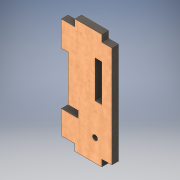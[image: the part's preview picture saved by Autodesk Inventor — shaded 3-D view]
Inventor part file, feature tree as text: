
AUTODESK INVENTOR PART (.ipt)
format: ipt  version: 2019 (Build 230136000, 136)  size: 162,816 bytes
history: native  units: mm
features: extrude x3, sketch x3, other x1
ambient origin geometry x8: Origin, YZ Plane, XZ Plane, XY Plane, X Axis, Y Axis, Z Axis, Center Point
bodies: Body1 (feature_tree)
feature tree (7):
  other  "Твердое тело1"
  extrude  "Выдавливание1"  Depth=16.0mm
  extrude  "Выдавливание2"  Depth=8.0mm
  extrude  "Выдавливание3"  Depth=4.0mm TaperAngle=0.0deg
  sketch  "Эскиз1"
  sketch  "Эскиз2"
  sketch  "Эскиз3"
